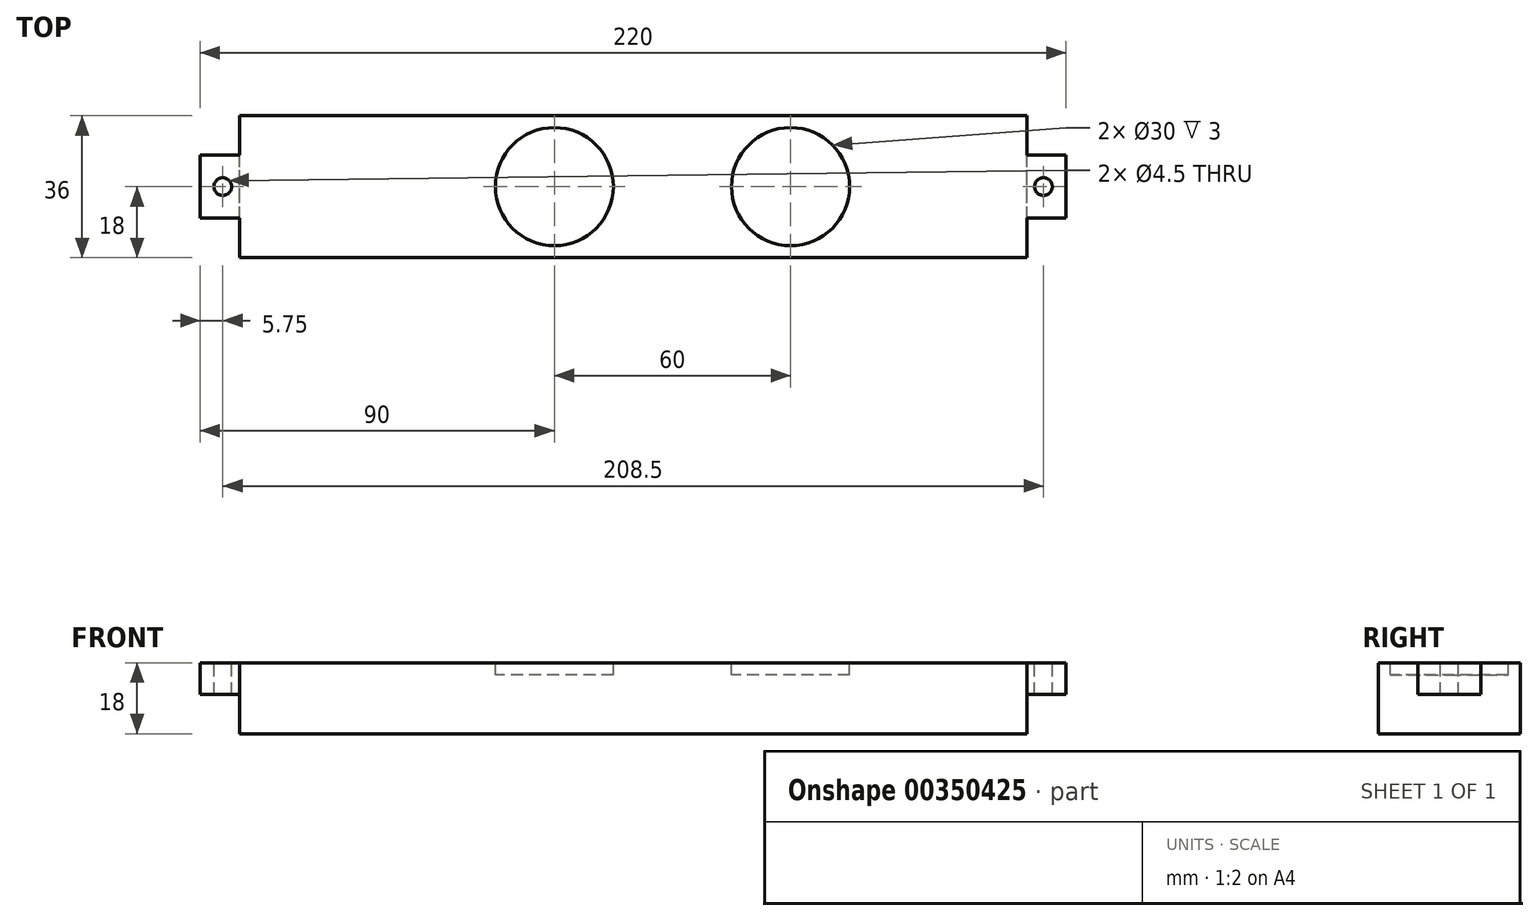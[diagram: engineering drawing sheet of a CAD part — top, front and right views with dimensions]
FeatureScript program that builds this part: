
annotation { "Feature Type Name" : "Feature", "Feature Type Description" : "" }
export const myFeature = defineFeature(function(context is Context, id is Id, definition is map)
    precondition{}
    {
        {
            var Q0;
            Q0=qCreatedBy(makeId("Top.planeOp"),FACE);
            var sketch = newSketch(context, id + "F0", { "sketchPlane" : qUnion([Q0])});
            skLineSegment(sketch, "E0.bottom", {"start": v(100, -18) * mm, "end": v(-100, -18) * mm});
            skLineSegment(sketch, "E0.top", {"start": v(100, 18) * mm, "end": v(-100, 18) * mm});
            skLineSegment(sketch, "E0.left", {"start": v(100, -18) * mm, "end": v(100, 18) * mm});
            skLineSegment(sketch, "E0.right", {"start": v(-100, -18) * mm, "end": v(-100, 18) * mm});
            skPoint(sketch, "E0.middle", {"position": v(0, 0) * mm});
            skSolve(sketch);
        }
        {
            var Q0;
            Q0 = qSketchRegion(id + "F0", true);
            extrude(context, id + "F1", {"entities" : qUnion([Q0]), "depth" : 18 * mm});
        }
        {
            var Q0;
            Q0=makeQuery(id+"F1.opExtrude","CAP_FACE",FACE,{"disambiguationData":[OSD([sQuery(id+"F0.wireOp",EDGE,"E0.bottom"),sQuery(id+"F0.wireOp",EDGE,"E0.top"),sQuery(id+"F0.wireOp",EDGE,"E0.left"),sQuery(id+"F0.wireOp",EDGE,"E0.right")])],"isStart":false});
            var sketch = newSketch(context, id + "F2", { "sketchPlane" : qUnion([Q0])});
            skCircle(sketch, "E1", {"center": v(-20, 0) * mm, "radius": 15 * mm});
            skCircle(sketch, "E2", {"center": v(40, 0) * mm, "radius": 15 * mm});
            skSolve(sketch);
        }
        {
            var Q0;
            Q0 = qSketchRegion(id + "F2", true);
            extrude(context, id + "F3", {"entities" : qUnion([Q0]), "operationType" : NewBodyOperationType.REMOVE, "oppositeDirection" : true, "depth" : 3 * mm});
        }
        {
            var Q0;
            Q0=makeQuery(id+"F1.opExtrude","CAP_FACE",FACE,{"disambiguationData":[OSD([sQuery(id+"F0.wireOp",EDGE,"E0.bottom"),sQuery(id+"F0.wireOp",EDGE,"E0.top"),sQuery(id+"F0.wireOp",EDGE,"E0.left"),sQuery(id+"F0.wireOp",EDGE,"E0.right")])],"isStart":false});
            var sketch = newSketch(context, id + "F4", { "sketchPlane" : qUnion([Q0])});
            skLineSegment(sketch, "E3.bottom", {"start": v(-100, -8) * mm, "end": v(-110, -8) * mm});
            skLineSegment(sketch, "E3.top", {"start": v(-100, 8) * mm, "end": v(-110, 8) * mm});
            skLineSegment(sketch, "E3.left", {"start": v(-100, -8) * mm, "end": v(-100, 8) * mm});
            skLineSegment(sketch, "E3.right", {"start": v(-110, -8) * mm, "end": v(-110, 8) * mm});
            skPoint(sketch, "E4.firstSnap0", {"position": v(-105, -8) * mm});
            skPoint(sketch, "E4.oppositeSnap0", {"position": v(-105, 8) * mm});
            skLineSegment(sketch, "E4.bottom", {"start": v(100, -8) * mm, "end": v(110, -8) * mm});
            skLineSegment(sketch, "E4.top", {"start": v(100, 8) * mm, "end": v(110, 8) * mm});
            skLineSegment(sketch, "E4.left", {"start": v(100, -8) * mm, "end": v(100, 8) * mm});
            skLineSegment(sketch, "E4.right", {"start": v(110, -8) * mm, "end": v(110, 8) * mm});
            skCircle(sketch, "E5", {"center": v(-104.25, 0) * mm, "radius": 2.25 * mm});
            skCircle(sketch, "E6", {"center": v(104.25, 0) * mm, "radius": 2.25 * mm});
            skSolve(sketch);
        }
        {
            var Q0;
            Q0 = qSketchRegion(id + "F4", true);
            extrude(context, id + "F5", {"entities" : qUnion([Q0]), "operationType" : NewBodyOperationType.ADD, "oppositeDirection" : true, "depth" : 8 * mm});
        }
    });
